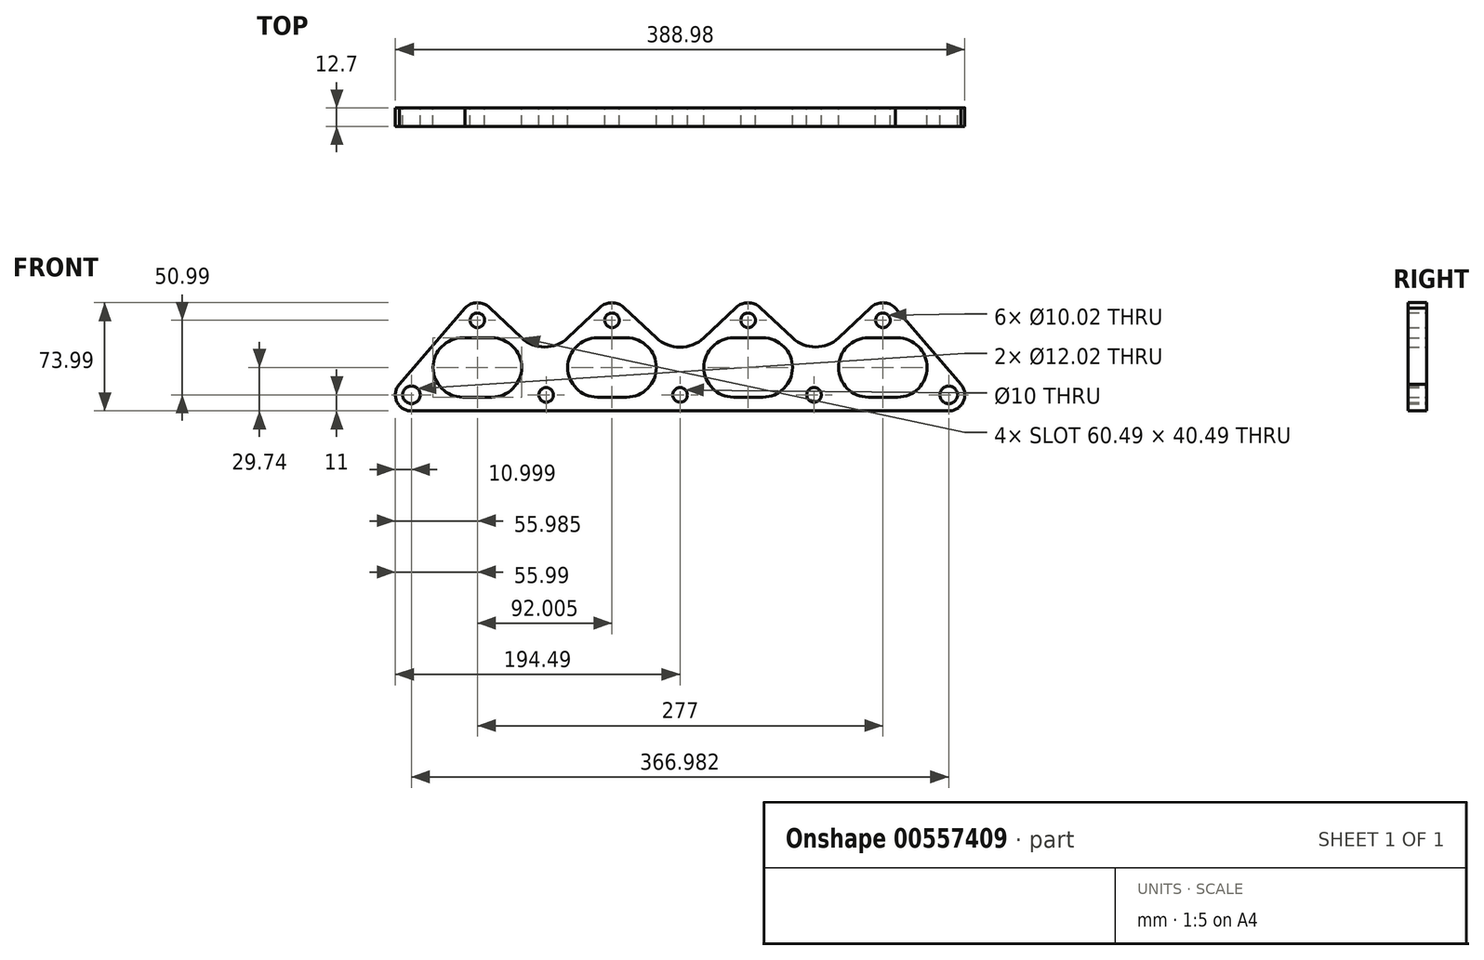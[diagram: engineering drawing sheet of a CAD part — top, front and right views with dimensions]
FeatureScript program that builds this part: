
annotation { "Feature Type Name" : "Feature", "Feature Type Description" : "" }
export const myFeature = defineFeature(function(context is Context, id is Id, definition is map)
    precondition{}
    {
        {
            var Q0;
            Q0=qCreatedBy(makeId("Front.planeOp"),FACE);
            var sketch = newSketch(context, id + "F0", { "sketchPlane" : qUnion([Q0])});
            skCircle(sketch, "E0", {"center": v(275, 11) * mm, "radius": 5 * mm});
            skCircle(sketch, "E1", {"center": v(367, 11) * mm, "radius": 6.01 * mm});
            skCircle(sketch, "E2", {"center": v(230, 62) * mm, "radius": 5.01 * mm});
            skCircle(sketch, "E3", {"center": v(322, 62) * mm, "radius": 5.01 * mm});
            skArc(sketch, "E4", {"start": v(367, 0) * mm, "mid": v(377.02, 6.47) * mm, "end": v(375.25, 18.27) * mm});
            skLineSegment(sketch, "E5", {"start": v(330.49, 70.48) * mm, "end": v(375.25, 18.27) * mm});
            skLineSegment(sketch, "E6", {"start": v(220, 9.5) * mm, "end": v(240, 9.5) * mm});
            skLineSegment(sketch, "E7", {"start": v(220, 50) * mm, "end": v(240, 50) * mm});
            skArc(sketch, "E8", {"start": v(220, 9.5) * mm, "mid": v(199.75, 29.75) * mm, "end": v(220, 50) * mm});
            skArc(sketch, "E9", {"start": v(240, 50) * mm, "mid": v(260.25, 29.75) * mm, "end": v(240, 9.5) * mm});
            skLineSegment(sketch, "E10", {"start": v(332, 9.5) * mm, "end": v(312, 9.5) * mm});
            skLineSegment(sketch, "E11", {"start": v(312, 49.98) * mm, "end": v(332, 49.98) * mm});
            skArc(sketch, "E12", {"start": v(312, 49.98) * mm, "mid": v(291.76, 29.74) * mm, "end": v(312, 9.5) * mm});
            skArc(sketch, "E13", {"start": v(332, 9.5) * mm, "mid": v(352.25, 29.74) * mm, "end": v(332, 49.98) * mm});
            skLineSegment(sketch, "E14", {"start": v(291.76, 49.98) * mm, "end": v(313.77, 70.72) * mm});
            skArc(sketch, "E15", {"start": v(291.76, 49.98) * mm, "mid": v(276, 43.73) * mm, "end": v(260.25, 49.98) * mm});
            skLineSegment(sketch, "E16", {"start": v(260.25, 49.98) * mm, "end": v(238.23, 70.73) * mm});
            skLineSegment(sketch, "E17", {"start": v(199.76, 50) * mm, "end": v(221.77, 70.73) * mm});
            skArc(sketch, "E18", {"start": v(221.77, 70.73) * mm, "mid": v(230, 74) * mm, "end": v(238.23, 70.73) * mm});
            skArc(sketch, "E19", {"start": v(313.77, 70.72) * mm, "mid": v(322.18, 73.99) * mm, "end": v(330.49, 70.48) * mm});
            skLineSegment(sketch, "E20", {"start": v(367, 0) * mm, "end": v(183.5, 0) * mm});
            skPoint(sketch, "E21.startSnap0", {"position": v(276, 43.73) * mm});
            skArc(sketch, "E22", {"start": v(183.5, 6) * mm, "mid": v(188.5, 11) * mm, "end": v(183.5, 16) * mm});
            skLineSegment(sketch, "E23.MirrorCS", {"start": v(0, 0) * mm, "end": v(183.5, 0) * mm});
            skArc(sketch, "E24.MirrorCS", {"start": v(183.5, 6) * mm, "mid": v(178.5, 11) * mm, "end": v(183.5, 16) * mm});
            skArc(sketch, "E25.MirrorCS", {"start": v(147, 9.5) * mm, "mid": v(167.25, 29.75) * mm, "end": v(147, 50) * mm});
            skLineSegment(sketch, "E26.MirrorCS", {"start": v(147, 9.5) * mm, "end": v(127, 9.5) * mm});
            skLineSegment(sketch, "E27.MirrorCS", {"start": v(147, 50) * mm, "end": v(127, 50) * mm});
            skArc(sketch, "E28.MirrorCS", {"start": v(127, 50) * mm, "mid": v(106.76, 29.75) * mm, "end": v(127, 9.5) * mm});
            skLineSegment(sketch, "E29.MirrorCS", {"start": v(167.24, 50) * mm, "end": v(145.23, 70.73) * mm});
            skArc(sketch, "E30.MirrorCS", {"start": v(145.23, 70.73) * mm, "mid": v(137, 74) * mm, "end": v(128.77, 70.73) * mm});
            skLineSegment(sketch, "E31.MirrorCS", {"start": v(106.75, 49.98) * mm, "end": v(128.77, 70.73) * mm});
            skArc(sketch, "E32.MirrorCS", {"start": v(75.24, 49.98) * mm, "mid": v(91, 43.73) * mm, "end": v(106.75, 49.98) * mm});
            skCircle(sketch, "E33.MirrorC", {"center": v(92, 11) * mm, "radius": 5 * mm});
            skLineSegment(sketch, "E34.MirrorCS", {"start": v(75.24, 49.98) * mm, "end": v(53.23, 70.72) * mm});
            skArc(sketch, "E35.MirrorCS", {"start": v(53.23, 70.72) * mm, "mid": v(44.82, 73.99) * mm, "end": v(36.51, 70.48) * mm});
            skLineSegment(sketch, "E36.MirrorCS", {"start": v(36.51, 70.48) * mm, "end": v(-8.25, 18.27) * mm});
            skArc(sketch, "E37.MirrorCS", {"start": v(0, 0) * mm, "mid": v(-10.02, 6.47) * mm, "end": v(-8.25, 18.27) * mm});
            skArc(sketch, "E38.MirrorCS", {"start": v(55, 49.98) * mm, "mid": v(75.24, 29.74) * mm, "end": v(55, 9.5) * mm});
            skLineSegment(sketch, "E39.MirrorCS", {"start": v(55, 49.98) * mm, "end": v(35, 49.98) * mm});
            skLineSegment(sketch, "E40.MirrorCS", {"start": v(35, 9.5) * mm, "end": v(55, 9.5) * mm});
            skArc(sketch, "E41.MirrorCS", {"start": v(35, 9.5) * mm, "mid": v(14.75, 29.74) * mm, "end": v(35, 49.98) * mm});
            skCircle(sketch, "E42.MirrorC", {"center": v(45, 62) * mm, "radius": 5.01 * mm});
            skCircle(sketch, "E43.MirrorC", {"center": v(137, 62) * mm, "radius": 5.01 * mm});
            skCircle(sketch, "E44.MirrorC", {"center": v(0, 11) * mm, "radius": 6.01 * mm});
            skArc(sketch, "E45", {"start": v(199.76, 50) * mm, "mid": v(183.5, 43.54) * mm, "end": v(167.24, 50) * mm});
            skSolve(sketch);
        }
        {
            var Q0;
            Q0 = qSketchRegion(id + "F0", true);
            extrude(context, id + "F1", {"entities" : qUnion([Q0]), "depth" : 12.7 * mm, "offsetDistance" : 25.4 * mm});
        }
    });
